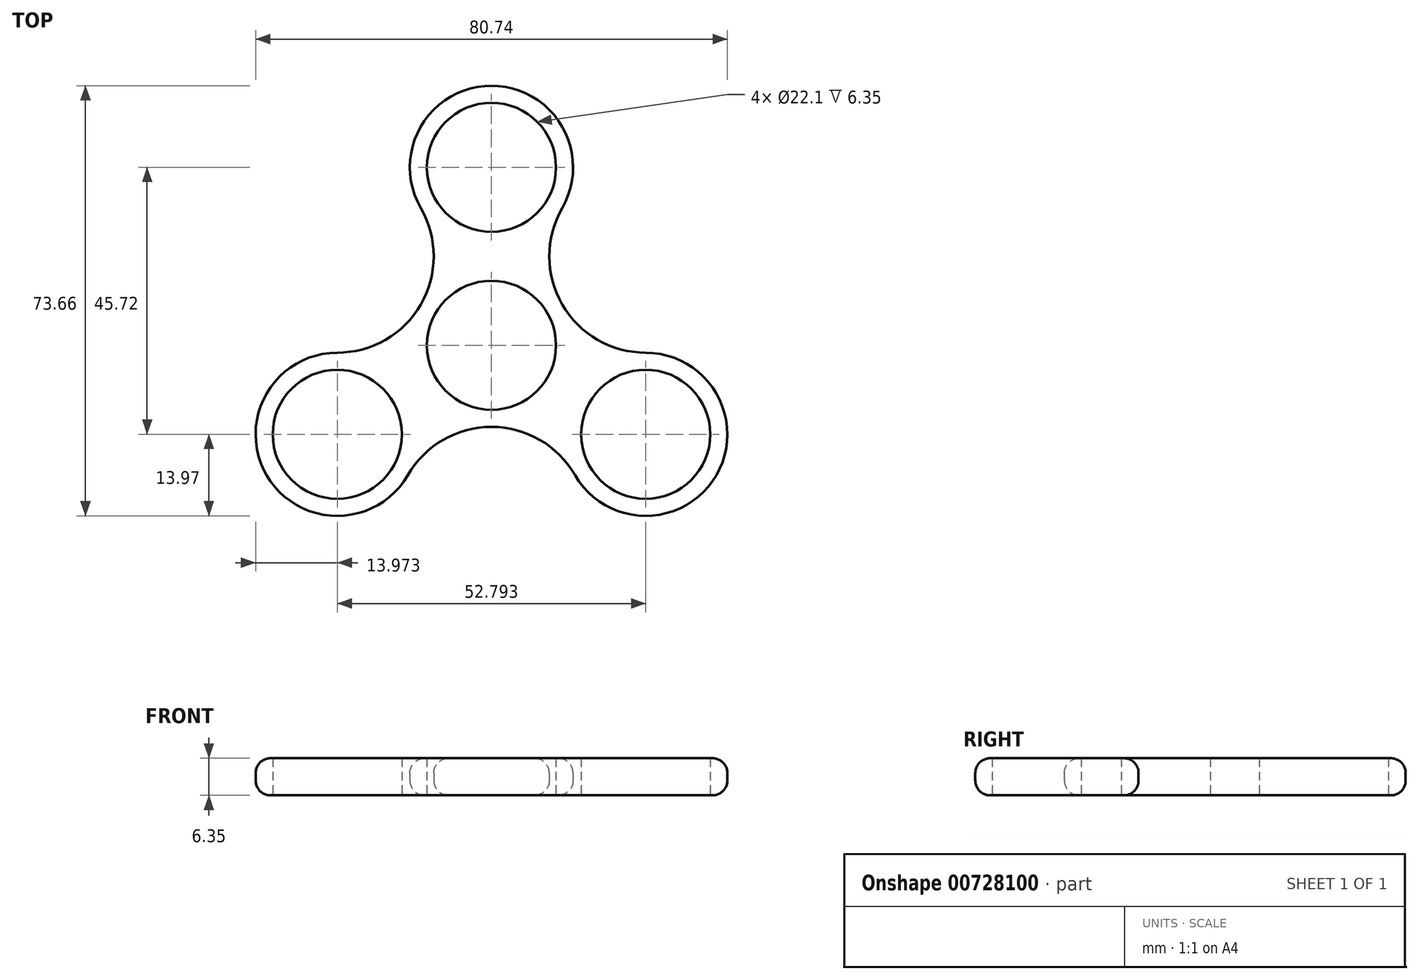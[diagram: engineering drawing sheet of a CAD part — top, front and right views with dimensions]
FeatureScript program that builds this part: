
annotation { "Feature Type Name" : "Feature", "Feature Type Description" : "" }
export const myFeature = defineFeature(function(context is Context, id is Id, definition is map)
    precondition{}
    {
        {
            var Q0;
            Q0=qCreatedBy(makeId("Top.planeOp"),FACE);
            var sketch = newSketch(context, id + "F0", { "sketchPlane" : qUnion([Q0])});
            skCircle(sketch, "E0", {"center": v(0, 0) * mm, "radius": 11.05 * mm});
            skCircle(sketch, "E1", {"center": v(0, 0) * mm, "radius": 13.97 * mm});
            skLineSegment(sketch, "E2", {"start": v(0, 0) * mm, "end": v(0, 30.48) * mm});
            skCircle(sketch, "E3", {"center": v(0, 30.48) * mm, "radius": 11.05 * mm});
            skCircle(sketch, "E4", {"center": v(0, 30.48) * mm, "radius": 13.97 * mm});
            skCircle(sketch, "E5.1.0", {"center": v(-26.4, -15.24) * mm, "radius": 11.05 * mm});
            skCircle(sketch, "E5.2.0", {"center": v(26.4, -15.24) * mm, "radius": 11.05 * mm});
            skCircle(sketch, "E6.1.0", {"center": v(-26.4, -15.24) * mm, "radius": 13.97 * mm});
            skCircle(sketch, "E6.2.0", {"center": v(26.4, -15.24) * mm, "radius": 13.97 * mm});
            skLineSegment(sketch, "E7", {"start": v(0, 0) * mm, "end": v(-26.4, 15.24) * mm});
            skArc(sketch, "E8", {"start": v(-26.4, -1.27) * mm, "mid": v(-12.1, 6.99) * mm, "end": v(-12.1, 23.5) * mm});
            skArc(sketch, "E9.1.0", {"start": v(14.3, -22.23) * mm, "mid": v(0, -13.97) * mm, "end": v(-14.3, -22.22) * mm});
            skArc(sketch, "E9.2.0", {"start": v(12.1, 23.5) * mm, "mid": v(12.1, 6.98) * mm, "end": v(26.4, -1.27) * mm});
            skSolve(sketch);
        }
        {
            var Q0;
            Q0=makeQuery(id+"F0.imprint","IMPRINT",FACE,{"disambiguationData":[TD([[makeQuery(id+"F0.imprint","IMPRINT",EDGE,{"derivedFrom":sQuery(id+"F0.wireOp",EDGE,"E3")}),-1.0]])]});
            var Q1;
            {var subQ0=sQuery(id+"F0.wireOp",EDGE,"E9.2.0");var subQ1=sQuery(id+"F0.wireOp",EDGE,"E1");var subQ2=makeQuery(id+"F0.imprint","INTERSECT",VERTEX,{"derivedFrom":[subQ1,subQ0]});Q1=makeQuery(id+"F0.imprint","IMPRINT",FACE,{"disambiguationData":[TD([[makeQuery(id+"F0.imprint","IMPRINT",EDGE,{"disambiguationData":[TD([[subQ2,-1.0]])],"derivedFrom":subQ1}),-1.0]])]});}
            var Q2;
            {var subQ5=sQuery(id+"F0.wireOp",EDGE,"E2");var subQ7=sQuery(id+"F0.wireOp",EDGE,"E0");var subQ8=makeQuery(id+"F0.imprint","INTERSECT",VERTEX,{"derivedFrom":[subQ7,subQ5]});Q2=makeQuery(id+"F0.imprint","IMPRINT",FACE,{"disambiguationData":[TD([[makeQuery(id+"F0.imprint","IMPRINT",EDGE,{"disambiguationData":[TD([[subQ8,1.0]])],"derivedFrom":subQ7}),-1.0]])]});}
            var Q3;
            {var subQ0=sQuery(id+"F0.wireOp",EDGE,"E2");var subQ5=sQuery(id+"F0.wireOp",EDGE,"E4");var subQ6=makeQuery(id+"F0.imprint","INTERSECT",VERTEX,{"derivedFrom":[subQ0,subQ5]});Q3=makeQuery(id+"F0.imprint","IMPRINT",FACE,{"disambiguationData":[TD([[makeQuery(id+"F0.imprint","IMPRINT",EDGE,{"disambiguationData":[TD([[subQ6,1.0]])],"derivedFrom":subQ0}),1.0]])]});}
            var Q4;
            {var subQ0=sQuery(id+"F0.wireOp",EDGE,"E2");var subQ1=sQuery(id+"F0.wireOp",EDGE,"E0");var subQ2=makeQuery(id+"F0.imprint","INTERSECT",VERTEX,{"derivedFrom":[subQ1,subQ0]});Q4=makeQuery(id+"F0.imprint","IMPRINT",FACE,{"disambiguationData":[TD([[makeQuery(id+"F0.imprint","IMPRINT",EDGE,{"disambiguationData":[TD([[subQ2,-1.0]])],"derivedFrom":subQ1}),-1.0]])]});}
            var Q5;
            {var subQ3=sQuery(id+"F0.wireOp",EDGE,"E8");var subQ5=sQuery(id+"F0.wireOp",EDGE,"E6.1.0");var subQ7=makeQuery(id+"F0.imprint","INTERSECT",VERTEX,{"derivedFrom":[subQ5,subQ3]});Q5=makeQuery(id+"F0.imprint","IMPRINT",FACE,{"disambiguationData":[TD([[makeQuery(id+"F0.imprint","IMPRINT",EDGE,{"disambiguationData":[TD([[subQ7,1.0]])],"derivedFrom":subQ5}),-1.0]])]});}
            var Q6;
            Q6=makeQuery(id+"F0.imprint","IMPRINT",FACE,{"disambiguationData":[TD([[makeQuery(id+"F0.imprint","IMPRINT",EDGE,{"derivedFrom":sQuery(id+"F0.wireOp",EDGE,"E5.1.0")}),-1.0]])]});
            var Q7;
            {var subQ0=sQuery(id+"F0.wireOp",EDGE,"E9.2.0");var subQ1=sQuery(id+"F0.wireOp",EDGE,"E1");var subQ2=makeQuery(id+"F0.imprint","INTERSECT",VERTEX,{"derivedFrom":[subQ1,subQ0]});Q7=makeQuery(id+"F0.imprint","IMPRINT",FACE,{"disambiguationData":[TD([[makeQuery(id+"F0.imprint","IMPRINT",EDGE,{"disambiguationData":[TD([[subQ2,1.0]])],"derivedFrom":subQ1}),-1.0]])]});}
            var Q8;
            Q8=makeQuery(id+"F0.imprint","IMPRINT",FACE,{"disambiguationData":[TD([[makeQuery(id+"F0.imprint","IMPRINT",EDGE,{"derivedFrom":sQuery(id+"F0.wireOp",EDGE,"E5.2.0")}),-1.0]])]});
            extrude(context, id + "F1", {"entities" : qUnion([Q0, Q1, Q2, Q3, Q4, Q5, Q6, Q7, Q8]), "depth" : 6.35 * mm, "offsetDistance" : 25.4 * mm});
        }
        {
            var Q0;
            Q0=makeQuery(id+"F1.opExtrude","CAP_EDGE",EDGE,{"disambiguationData":[OSD([sQuery(id+"F0.wireOp",EDGE,"E6.2.0")])],"isStart":true});
            var Q1;
            Q1=makeQuery(id+"F1.opExtrude","CAP_EDGE",EDGE,{"disambiguationData":[OSD([sQuery(id+"F0.wireOp",EDGE,"E8")])],"isStart":false});
            fillet(context, id + "F2", {"entities" : qUnion([Q0, Q1]), "radius" : 2.54 * mm, "tangentPropagation" : true, "allowEdgeOverflow" : false});
        }
    });
